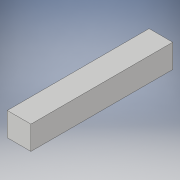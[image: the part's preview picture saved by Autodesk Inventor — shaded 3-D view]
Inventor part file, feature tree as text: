
AUTODESK INVENTOR PART (.ipt)
format: ipt  version: 2017 (Build 210142000, 142)  size: 87,552 bytes
history: native  units: in
note: dims shown in document units (in); Inventor stores cm internally (conversion verified against a paired STEP export)
features: extrude x1, sketch x1
ambient origin geometry x8: Origin, YZ Plane, XZ Plane, XY Plane, X Axis, Y Axis, Z Axis, Center Point
bodies: Solid1 (feature_tree)
feature tree (2):
  extrude  "Extrusion1"  Depth=2.0in
  sketch  "Sketch1"  dims[d0=2.0in d1=2.0in d2=12.0in d3=0.0in]
